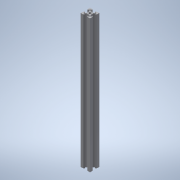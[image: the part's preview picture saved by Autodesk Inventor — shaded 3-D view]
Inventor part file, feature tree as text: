
AUTODESK INVENTOR PART (.ipt)
format: ipt  version: 2022.1 (Build 261234020, 234B)  size: 199,680 bytes
history: native  units: mm
features: extrude x1, sketch x1
ambient origin geometry x8: Origin, YZ Plane, XZ Plane, XY Plane, X Axis, Y Axis, Z Axis, Center Point
bodies: Body1 (feature_tree)
feature tree (2):
  extrude  "Extrusion9"  [1 undecoded]
  sketch  "Sketch1"  dims[d44=288.925mm d45=0.0mm]
note: 1 required parameter value undecoded (feature->parameter linkage not recoverable at this tier; creation-order binding heuristic only, values carry confidence <= 0.55)
